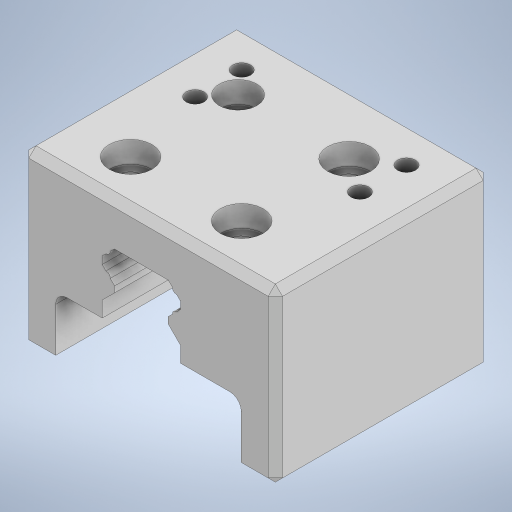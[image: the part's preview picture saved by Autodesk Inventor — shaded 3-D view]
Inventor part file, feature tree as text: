
AUTODESK INVENTOR PART (.ipt)
format: ipt  version: 2023 (Build 270158000, 158)  size: 401,408 bytes
history: native  units: in
note: dims shown in document units (in); Inventor stores cm internally (conversion verified against a paired STEP export)
features: extrude x7, sketch x3, thicken_offset x1, chamfer x1
ambient origin geometry x8: Origin, YZ Plane, XZ Plane, XY Plane, X Axis, Y Axis, Z Axis, Center Point
bodies: Solid1 (feature_tree)
feature tree (12):
  extrude  "Extrusion1"  Depth=2.3622in
  extrude  "Extrusion2"  Depth=0.0197in
  extrude  "Extrusion3"  Depth=0.0787in
  extrude  "Extrusion4"  Depth=0.1969in
  extrude  "Extrusion5"  Depth=0.0787in
  extrude  "Extrusion6"  Depth=0.5118in
  extrude  "Extrusion9"  Depth=2.7874in
  thicken_offset  "Thicken1"
  chamfer  "Chamfer1"  Distance=2.3622in
  sketch  "Sketch4"  dims[d0=0.9843in d1=2.3622in]
  sketch  "Sketch5"  dims[d2=0.0197in d3=0.0197in]
  sketch  "Sketch8"  dims[d4=0.0197in d5=0.0197in d6=0.1969in d7=1.811in d8=0.5118in d9=2.7874in d10=2.3622in d11=1.3937in d12=0.0in d13=1.3937in d14=0.0in d15=0.3937in d16=0.1969in d17=0.0in d18=0.0in d19=0.3937in d20=1.1969in d21=0.0in d22=0.0in d27=0.3937in d28=0.0in d29=0.2687in d31=1.4375in d32=0.0in d34=0.4724in d35=0.2362in d36=0.0in d50=1.3937in d51=0.0394in d52=0.1181in d53=135.0deg d54=0.0787in d55=0.1358in d56=0.689in d57=0.2819in d58=0.0935in d59=0.0525in d60=0.0953in d61=0.3937in d63=0.3937in d64=0.0in d66=0.0394in d67=0.125in d68=0.374in d69=0.689in d70=90.0deg d71=90.0deg d72=0.7874in d73=0.0354in d74=0.689in d78=1.1811in d79=1.2205in d80=0.689in d81=0.0787in d82=0.0787in d83=45.0deg d84=0.2953in d85=0.0787in d86=1.315in d87=0.4134in]
